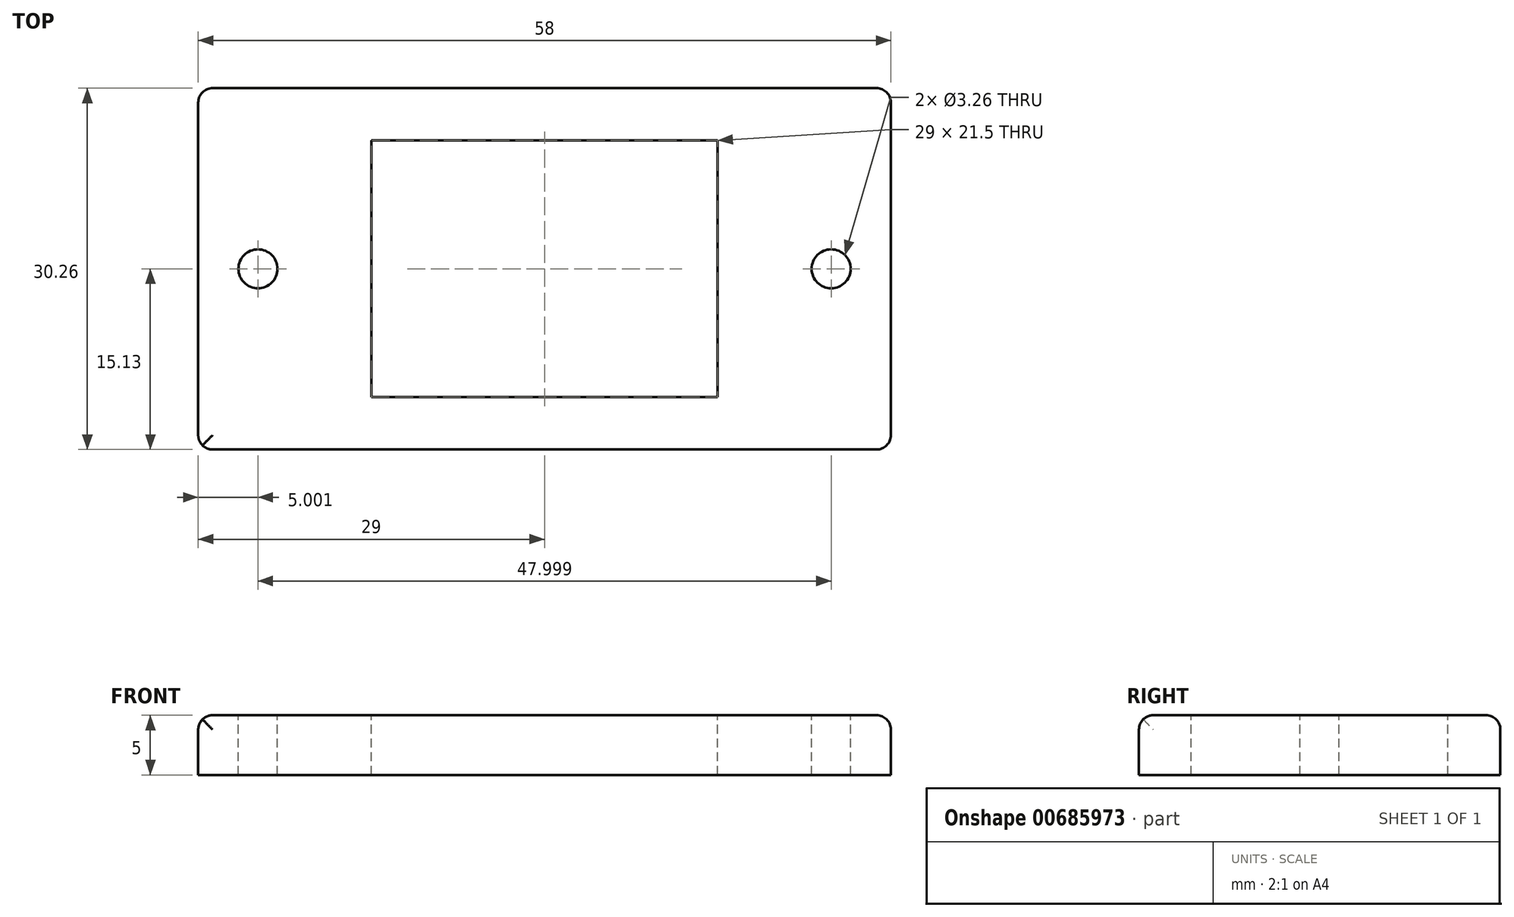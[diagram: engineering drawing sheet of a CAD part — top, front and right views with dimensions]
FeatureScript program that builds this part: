
annotation { "Feature Type Name" : "Feature", "Feature Type Description" : "" }
export const myFeature = defineFeature(function(context is Context, id is Id, definition is map)
    precondition{}
    {
        {
            var Q0;
            Q0=qCreatedBy(makeId("Top.planeOp"),FACE);
            var sketch = newSketch(context, id + "F0", { "sketchPlane" : qUnion([Q0])});
            skLineSegment(sketch, "E0.bottom", {"start": v(-29, 15.13) * mm, "end": v(29, 15.13) * mm});
            skLineSegment(sketch, "E0.top", {"start": v(-29, -15.13) * mm, "end": v(29, -15.13) * mm});
            skLineSegment(sketch, "E0.left", {"start": v(-29, 15.13) * mm, "end": v(-29, -15.13) * mm});
            skLineSegment(sketch, "E0.right", {"start": v(29, 15.13) * mm, "end": v(29, -15.13) * mm});
            skPoint(sketch, "E0.middle", {"position": v(0, 0) * mm});
            skSolve(sketch);
        }
        {
            var Q0;
            Q0=makeQuery(id+"F0.imprint","IMPRINT",FACE,{"disambiguationData":[TD([[makeQuery(id+"F0.imprint","IMPRINT",EDGE,{"derivedFrom":sQuery(id+"F0.wireOp",EDGE,"E0.bottom")}),-1.0]])]});
            extrude(context, id + "F1", {"entities" : qUnion([Q0]), "oppositeDirection" : true, "depth" : 5 * mm, "offsetDistance" : 25 * mm});
        }
        {
            var Q0;
            Q0=qCreatedBy(makeId("Top.planeOp"),FACE);
            var sketch = newSketch(context, id + "F2", { "sketchPlane" : qUnion([Q0])});
            skPoint(sketch, "E1", {"position": v(-24, 0) * mm});
            skPoint(sketch, "E2", {"position": v(24, 0) * mm});
            skSolve(sketch);
        }
        {
            var Q0;
            Q0=sQuery(id+"F2.wireOp",VERTEX,"E1");
            var Q1;
            Q1=sQuery(id+"F2.wireOp",VERTEX,"E2");
            var Q2;
            Q2=makeQuery(id+"F1.opExtrude","SWEPT_BODY",BODY,{"disambiguationData":[OSD([sQuery(id+"F0.wireOp",EDGE,"E0.bottom"),sQuery(id+"F0.wireOp",EDGE,"E0.top"),sQuery(id+"F0.wireOp",EDGE,"E0.left"),sQuery(id+"F0.wireOp",EDGE,"E0.right")])]});
            hole(context, id + "F3", {"style" : HoleStyle.SIMPLE, "endStyle" : HoleEndStyle.THROUGH, "standardTappedOrClearance" : lookupTablePath({ "standard" : "ANSI", "fit" : "Normal (ASME)", "size" : "#4", "type" : "Clearance" }), "standardBlindInLast" : lookupTablePath({ "fit" : "Free", "standard" : "ANSI", "size" : "#4", "type" : "Clearance" }), "holeDiameter" : 3.26 * mm, "majorDiameter" : 5 * mm, "isTappedThrough" : true, "tappedDepth" : 12 * mm, "tapClearance" : 3, "locations" : qUnion([Q0, Q1]), "scope" : qUnion([Q2])});
        }
        {
            var Q0;
            Q0=qCreatedBy(makeId("Top.planeOp"),FACE);
            var sketch = newSketch(context, id + "F4", { "sketchPlane" : qUnion([Q0])});
            skLineSegment(sketch, "E3.bottom", {"start": v(-14.5, 10.75) * mm, "end": v(14.5, 10.75) * mm});
            skLineSegment(sketch, "E3.top", {"start": v(-14.5, -10.75) * mm, "end": v(14.5, -10.75) * mm});
            skLineSegment(sketch, "E3.left", {"start": v(-14.5, 10.75) * mm, "end": v(-14.5, -10.75) * mm});
            skLineSegment(sketch, "E3.right", {"start": v(14.5, 10.75) * mm, "end": v(14.5, -10.75) * mm});
            skPoint(sketch, "E3.middle", {"position": v(0, 0) * mm});
            skSolve(sketch);
        }
        {
            var Q0;
            Q0=makeQuery(id+"F4.imprint","IMPRINT",FACE,{"disambiguationData":[TD([[makeQuery(id+"F4.imprint","IMPRINT",EDGE,{"derivedFrom":sQuery(id+"F4.wireOp",EDGE,"E3.bottom")}),-1.0]])]});
            extrude(context, id + "F5", {"entities" : qUnion([Q0]), "operationType" : NewBodyOperationType.REMOVE, "oppositeDirection" : true, "depth" : 25 * mm, "offsetDistance" : 25 * mm});
        }
        {
            var Q0;
            Q0=makeQuery(id+"F1.opExtrude","SWEPT_EDGE",EDGE,{"disambiguationData":[OSD([sQuery(id+"F0.wireOp",EDGE,"E0.top"),sQuery(id+"F0.wireOp",EDGE,"E0.left")])]});
            var Q1;
            Q1=makeQuery(id+"F1.opExtrude","CAP_EDGE",EDGE,{"disambiguationData":[OSD([sQuery(id+"F0.wireOp",EDGE,"E0.top")])],"isStart":true});
            fillet(context, id + "F6", {"entities" : qUnion([Q0, Q1]), "radius" : 1.2 * mm, "tangentPropagation" : true, "allowEdgeOverflow" : false});
        }
        {
            var Q0;
            Q0=makeQuery(id+"F1.opExtrude","CAP_EDGE",EDGE,{"disambiguationData":[OSD([sQuery(id+"F0.wireOp",EDGE,"E0.bottom")])],"isStart":true});
            fillet(context, id + "F7", {"entities" : qUnion([Q0]), "radius" : 1.2 * mm, "tangentPropagation" : true, "allowEdgeOverflow" : false});
        }
        {
            var Q0;
            Q0=makeQuery(id+"F1.opExtrude","CAP_EDGE",EDGE,{"disambiguationData":[OSD([sQuery(id+"F0.wireOp",EDGE,"E0.right")])],"isStart":true});
            fillet(context, id + "F8", {"entities" : qUnion([Q0]), "radius" : 1.2 * mm, "tangentPropagation" : true, "allowEdgeOverflow" : false});
        }
        {
            var Q0;
            Q0=makeQuery(id+"F1.opExtrude","CAP_EDGE",EDGE,{"disambiguationData":[OSD([sQuery(id+"F0.wireOp",EDGE,"E0.left")])],"isStart":true});
            fillet(context, id + "F9", {"entities" : qUnion([Q0]), "radius" : 1.2 * mm, "tangentPropagation" : true, "allowEdgeOverflow" : false});
        }
    });
